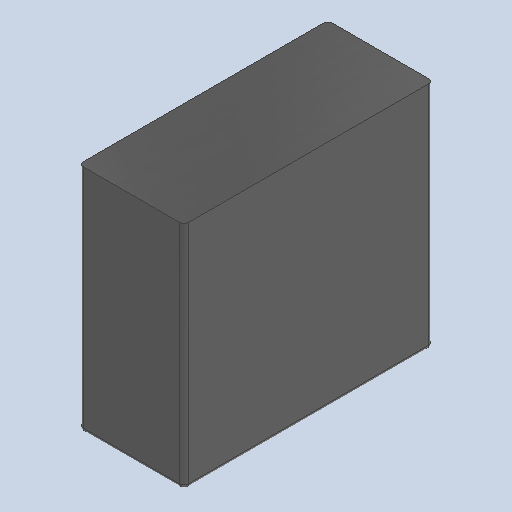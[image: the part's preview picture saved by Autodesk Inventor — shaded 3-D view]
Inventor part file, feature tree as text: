
AUTODESK INVENTOR PART (.ipt)
format: ipt  version: 2023 (Build 270158000, 158)  size: 214,528 bytes
history: native  units: in
note: dims shown in document units (in); Inventor stores cm internally (conversion verified against a paired STEP export)
features: extrude x1, fillet x1, shell x1, sketch x1
ambient origin geometry x8: Origin, YZ Plane, XZ Plane, XY Plane, X Axis, Y Axis, Z Axis, Center Point
bodies: Solid1 (feature_tree)
feature tree (4):
  extrude  "Extrusion1"  Depth=7.1in
  fillet  "Fillet1"  Radius=3.0in
  shell  "Shell1"  Thickness=0.125in
  sketch  "Sketch1"  dims[d0=6.58in d1=7.1in d2=3.0in d3=0.0in d4=0.125in d5=0.4in]
